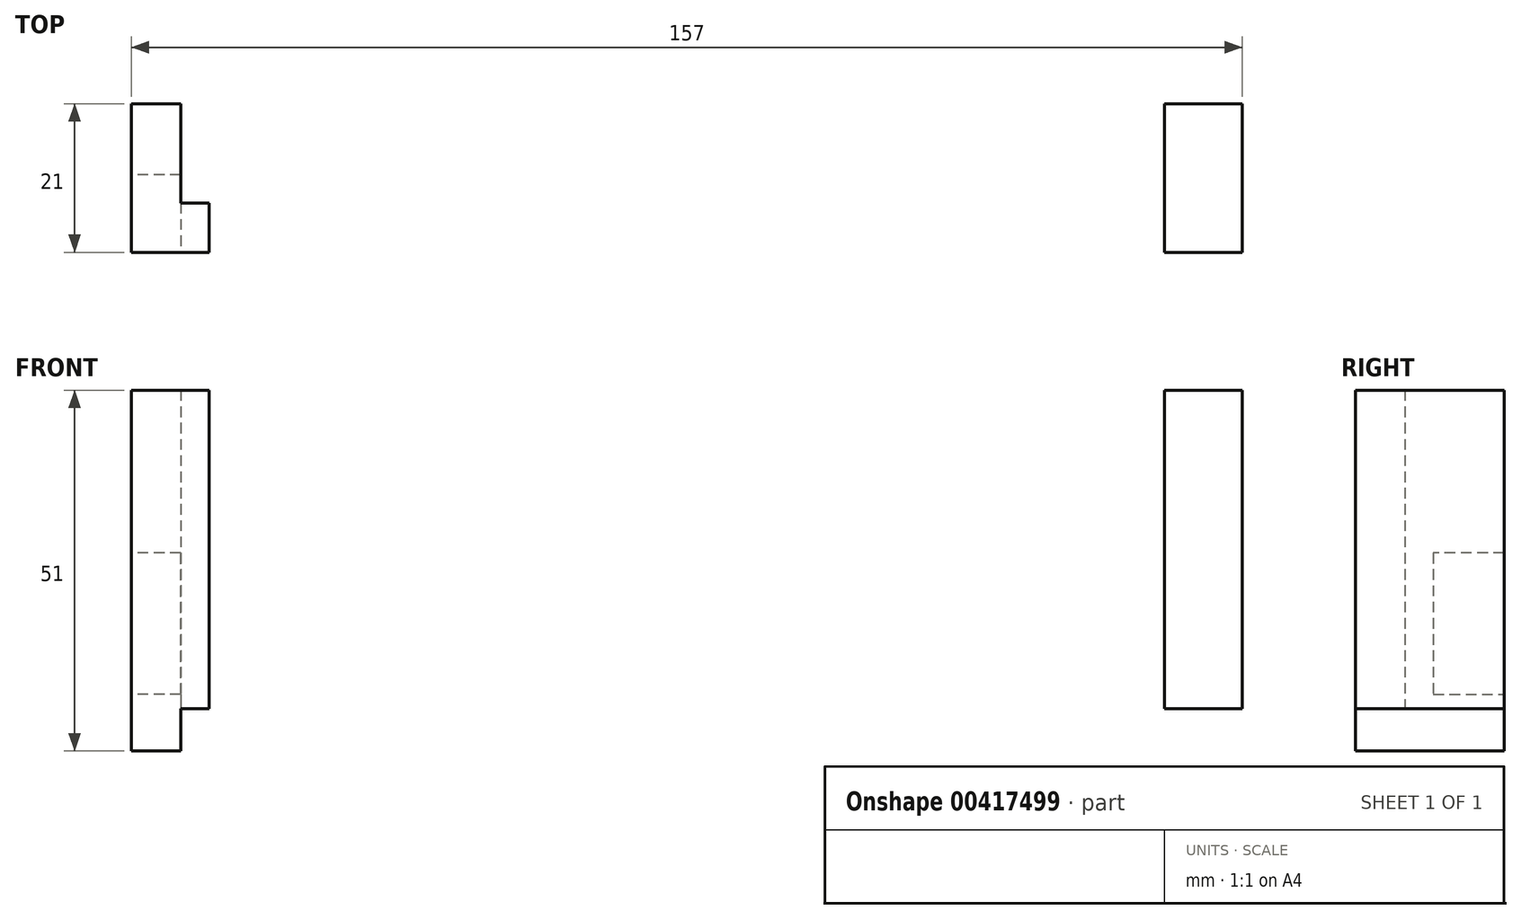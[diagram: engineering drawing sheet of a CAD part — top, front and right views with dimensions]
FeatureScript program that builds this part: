
annotation { "Feature Type Name" : "Feature", "Feature Type Description" : "" }
export const myFeature = defineFeature(function(context is Context, id is Id, definition is map)
    precondition{}
    {
        {
            var Q0;
            Q0=qCreatedBy(makeId("Front.planeOp"),FACE);
            var sketch = newSketch(context, id + "F0", { "sketchPlane" : qUnion([Q0])});
            skLineSegment(sketch, "E0.bottom", {"start": v(74.5, 22.5) * mm, "end": v(-74.5, 22.5) * mm});
            skLineSegment(sketch, "E0.top", {"start": v(74.5, -22.5) * mm, "end": v(-74.5, -22.5) * mm});
            skLineSegment(sketch, "E0.left", {"start": v(74.5, 22.5) * mm, "end": v(74.5, -22.5) * mm});
            skLineSegment(sketch, "E0.right", {"start": v(-74.5, 22.5) * mm, "end": v(-74.5, -22.5) * mm});
            skPoint(sketch, "E0.middle", {"position": v(0, 0) * mm});
            skLineSegment(sketch, "E1.0", {"start": v(78.5, 22.5) * mm, "end": v(78.5, -22.5) * mm});
            skLineSegment(sketch, "E2.0", {"start": v(-78.5, 22.5) * mm, "end": v(-78.5, -22.5) * mm});
            skLineSegment(sketch, "E3", {"start": v(-78.5, -22.5) * mm, "end": v(-74.5, -22.5) * mm});
            skLineSegment(sketch, "E4", {"start": v(74.5, -22.5) * mm, "end": v(78.5, -22.5) * mm});
            skLineSegment(sketch, "E5", {"start": v(78.5, 22.5) * mm, "end": v(74.5, 22.5) * mm});
            skLineSegment(sketch, "E6", {"start": v(-74.5, 22.5) * mm, "end": v(-78.5, 22.5) * mm});
            skLineSegment(sketch, "E7", {"start": v(0, -22.5) * mm, "end": v(67.5, -22.5) * mm});
            skLineSegment(sketch, "E8", {"start": v(67.5, -22.5) * mm, "end": v(67.5, 22.5) * mm});
            skLineSegment(sketch, "E9", {"start": v(0, -22.5) * mm, "end": v(-67.5, -22.5) * mm});
            skLineSegment(sketch, "E10", {"start": v(-67.5, -22.5) * mm, "end": v(-67.5, 22.5) * mm});
            skSolve(sketch);
        }
        {
            var Q0;
            Q0=makeQuery(id+"F0.imprint","IMPRINT",FACE,{"disambiguationData":[TD([[makeQuery(id+"F0.imprint","IMPRINT",EDGE,{"derivedFrom":sQuery(id+"F0.wireOp",EDGE,"E0.bottom")}),1.0]])]});
            var Q1;
            Q1=makeQuery(id+"F0.imprint","IMPRINT",FACE,{"disambiguationData":[TD([[makeQuery(id+"F0.imprint","IMPRINT",EDGE,{"derivedFrom":sQuery(id+"F0.wireOp",EDGE,"E0.right")}),-1.0]])]});
            var Q2;
            Q2=makeQuery(id+"F0.imprint","IMPRINT",FACE,{"disambiguationData":[TD([[makeQuery(id+"F0.imprint","IMPRINT",EDGE,{"derivedFrom":sQuery(id+"F0.wireOp",EDGE,"E0.left")}),1.0]])]});
            var Q3;
            Q3=makeQuery(id+"F0.imprint","IMPRINT",FACE,{"disambiguationData":[TD([[makeQuery(id+"F0.imprint","IMPRINT",EDGE,{"derivedFrom":sQuery(id+"F0.wireOp",EDGE,"E7")}),1.0]])]});
            extrude(context, id + "F1", {"entities" : qUnion([Q0, Q1, Q2, Q3]), "oppositeDirection" : true, "depth" : 18 * mm});
        }
        {
            var Q0;
            Q0=makeQuery(id+"F1.opExtrude","SWEPT_FACE",FACE,{"disambiguationData":[OSD([sQuery(id+"F0.wireOp",EDGE,"E0.top")])]});
            var sketch = newSketch(context, id + "F2", { "sketchPlane" : qUnion([Q0])});
            skLineSegment(sketch, "E11", {"start": v(-78.5, -9) * mm, "end": v(-74.5, -9) * mm, "construction": true});
            skLineSegment(sketch, "E12", {"start": v(78.5, -9) * mm, "end": v(74.5, -9) * mm, "construction": true});
            skLineSegment(sketch, "E13", {"start": v(74.5, 0) * mm, "end": v(74.5, -18) * mm, "construction": true});
            skLineSegment(sketch, "E14", {"start": v(-74.5, -18) * mm, "end": v(-74.5, 0) * mm, "construction": true});
            skLineSegment(sketch, "E15", {"start": v(74.5, -18) * mm, "end": v(71.5, -18) * mm});
            skLineSegment(sketch, "E16", {"start": v(71.5, -18) * mm, "end": v(71.5, 0) * mm});
            skLineSegment(sketch, "E17", {"start": v(-74.5, -18) * mm, "end": v(-71.5, -18) * mm});
            skLineSegment(sketch, "E18", {"start": v(-71.5, -18) * mm, "end": v(-71.5, 0) * mm});
            skLineSegment(sketch, "E19", {"start": v(-74.5, -18) * mm, "end": v(-74.5, -4) * mm, "construction": true});
            skLineSegment(sketch, "E20", {"start": v(-74.5, -4) * mm, "end": v(-71.5, -4) * mm, "construction": true});
            skLineSegment(sketch, "E21", {"start": v(-71.5, -4) * mm, "end": v(71.5, -4) * mm});
            skSolve(sketch);
        }
        {
            var Q0;
            {var subQ3=sQuery(id+"F2.wireOp",EDGE,"E21");Q0=makeQuery(id+"F2.imprint","IMPRINT",FACE,{"disambiguationData":[TD([[makeQuery(id+"F2.imprint","IMPRINT",EDGE,{"derivedFrom":subQ3}),-1.0]])]});}
            extrude(context, id + "F3", {"entities" : qUnion([Q0]), "operationType" : NewBodyOperationType.REMOVE, "oppositeDirection" : true, "depth" : 55 * mm});
        }
        {
            var Q0;
            {var subQ7=sQuery(id+"F2.wireOp",EDGE,"E17");Q0=makeQuery(id+"F2.imprint","IMPRINT",FACE,{"disambiguationData":[TD([[makeQuery(id+"F2.imprint","IMPRINT",EDGE,{"derivedFrom":subQ7}),-1.0]])]});}
            extrude(context, id + "F4", {"entities" : qUnion([Q0]), "operationType" : NewBodyOperationType.ADD, "depth" : 6 * mm});
        }
        {
            var Q0;
            {var subQ0=sQuery(id+"F0.wireOp",EDGE,"E2.0");Q0=makeQuery(id+"F4.boolean.opBoolean","MERGE",FACE,{"derivedFrom":[makeQuery(id+"F1.opExtrude","SWEPT_FACE",FACE,{"disambiguationData":[OSD([subQ0])]}),makeQuery(id+"F4.opExtrude","SWEPT_FACE",FACE,{"disambiguationData":[OSD([subQ0,sQuery(id+"F0.wireOp",EDGE,"E3")])]})]});}
            var sketch = newSketch(context, id + "F5", { "sketchPlane" : qUnion([Q0])});
            skLineSegment(sketch, "E22", {"start": v(-18, -28.5) * mm, "end": v(-18, -20.5) * mm, "construction": true});
            skLineSegment(sketch, "E23", {"start": v(-18, -20.5) * mm, "end": v(0, -20.5) * mm, "construction": true});
            skLineSegment(sketch, "E24", {"start": v(-18, -20.5) * mm, "end": v(-18, -0.5) * mm});
            skLineSegment(sketch, "E25", {"start": v(-18, -0.5) * mm, "end": v(-8, -0.5) * mm});
            skLineSegment(sketch, "E26", {"start": v(-8, -0.5) * mm, "end": v(-8, -20.5) * mm});
            skPoint(sketch, "E26.endSnap0", {"position": v(-9, -20.5) * mm});
            skLineSegment(sketch, "E27", {"start": v(-8, -20.5) * mm, "end": v(-18, -20.5) * mm});
            skSolve(sketch);
        }
        {
            var Q0;
            Q0=makeQuery(id+"F5.imprint","IMPRINT",FACE,{"disambiguationData":[TD([[makeQuery(id+"F5.imprint","IMPRINT",EDGE,{"derivedFrom":sQuery(id+"F5.wireOp",EDGE,"E24")}),1.0]])]});
            extrude(context, id + "F6", {"entities" : qUnion([Q0]), "operationType" : NewBodyOperationType.REMOVE, "oppositeDirection" : true, "depth" : 25 * mm});
        }
        {
            var Q0;
            {var subQ0=sQuery(id+"F0.wireOp",EDGE,"E0.left");Q0=makeQuery(id+"F0.imprint","IMPRINT",FACE,{"disambiguationData":[TD([[makeQuery(id+"F0.imprint","IMPRINT",EDGE,{"derivedFrom":subQ0}),-1.0]])]});}
            var Q1;
            Q1=makeQuery(id+"F0.imprint","IMPRINT",FACE,{"disambiguationData":[TD([[makeQuery(id+"F0.imprint","IMPRINT",EDGE,{"derivedFrom":sQuery(id+"F0.wireOp",EDGE,"E0.left")}),1.0]])]});
            var Q2;
            {var subQ0=sQuery(id+"F0.wireOp",EDGE,"E0.right");Q2=makeQuery(id+"F0.imprint","IMPRINT",FACE,{"disambiguationData":[TD([[makeQuery(id+"F0.imprint","IMPRINT",EDGE,{"derivedFrom":subQ0}),1.0]])]});}
            var Q3;
            Q3=makeQuery(id+"F0.imprint","IMPRINT",FACE,{"disambiguationData":[TD([[makeQuery(id+"F0.imprint","IMPRINT",EDGE,{"derivedFrom":sQuery(id+"F0.wireOp",EDGE,"E0.right")}),-1.0]])]});
            extrude(context, id + "F7", {"entities" : qUnion([Q0, Q1, Q2, Q3]), "depth" : 3 * mm});
        }
        {
            var Q0;
            Q0=makeQuery(id+"F7.opExtrude","SWEPT_BODY",BODY,{"disambiguationData":[OSD([sQuery(id+"F0.wireOp",EDGE,"E0.bottom"),sQuery(id+"F0.wireOp",EDGE,"E0.top"),sQuery(id+"F0.wireOp",EDGE,"E1.0"),sQuery(id+"F0.wireOp",EDGE,"E4"),sQuery(id+"F0.wireOp",EDGE,"E5"),sQuery(id+"F0.wireOp",EDGE,"E8")])]});
            var Q1;
            Q1=makeQuery(id+"F1.opExtrude","SWEPT_BODY",BODY,{"disambiguationData":[OSD([sQuery(id+"F0.wireOp",EDGE,"E0.bottom"),sQuery(id+"F0.wireOp",EDGE,"E0.top"),sQuery(id+"F0.wireOp",EDGE,"E1.0"),sQuery(id+"F0.wireOp",EDGE,"E2.0"),sQuery(id+"F0.wireOp",EDGE,"E3"),sQuery(id+"F0.wireOp",EDGE,"E4"),sQuery(id+"F0.wireOp",EDGE,"E5"),sQuery(id+"F0.wireOp",EDGE,"E6"),sQuery(id+"F0.wireOp",EDGE,"E7"),sQuery(id+"F0.wireOp",EDGE,"E9")])]});
            var Q2;
            Q2=makeQuery(id+"F7.opExtrude","SWEPT_BODY",BODY,{"disambiguationData":[OSD([sQuery(id+"F0.wireOp",EDGE,"E0.bottom"),sQuery(id+"F0.wireOp",EDGE,"E0.top"),sQuery(id+"F0.wireOp",EDGE,"E2.0"),sQuery(id+"F0.wireOp",EDGE,"E3"),sQuery(id+"F0.wireOp",EDGE,"E6"),sQuery(id+"F0.wireOp",EDGE,"E10")])]});
            booleanBodies(context, id + "F8", {"operationType" : BooleanOperationType.UNION, "tools" : qUnion([Q0, Q1, Q2])});
        }
        {
            var Q0;
            {var subQ1=sQuery(id+"F0.wireOp",EDGE,"E9");var subQ2=sQuery(id+"F0.wireOp",EDGE,"E7");var subQ3=sQuery(id+"F0.wireOp",EDGE,"E4");var subQ4=sQuery(id+"F0.wireOp",EDGE,"E3");var subQ5=sQuery(id+"F0.wireOp",EDGE,"E2.0");var subQ6=sQuery(id+"F0.wireOp",EDGE,"E0.top");Q0=makeQuery(id+"F8.opBoolean","SPLIT",FACE,{"disambiguationData":[TD([makeQuery(id+"F1.opExtrude","SWEPT_FACE",FACE,{"disambiguationData":[OSD([subQ5])]})])],"derivedFrom":makeQuery(id+"F4.boolean.opBoolean","MERGE",FACE,{"derivedFrom":[makeQuery(id+"F1.opExtrude","CAP_FACE",FACE,{"disambiguationData":[OSD([sQuery(id+"F0.wireOp",EDGE,"E0.bottom"),subQ6,sQuery(id+"F0.wireOp",EDGE,"E1.0"),subQ5,subQ4,subQ3,sQuery(id+"F0.wireOp",EDGE,"E5"),sQuery(id+"F0.wireOp",EDGE,"E6"),subQ2,subQ1])],"isStart":true}),makeQuery(id+"F4.opExtrude","SWEPT_FACE",FACE,{"disambiguationData":[OSD([subQ6,subQ4,subQ3,subQ2,subQ1])]})]})});}
            var sketch = newSketch(context, id + "F9", { "sketchPlane" : qUnion([Q0])});
            skLineSegment(sketch, "E28", {"start": v(-78.5, -28.5) * mm, "end": v(-71.5, -28.5) * mm});
            skLineSegment(sketch, "E29", {"start": v(-71.5, -28.5) * mm, "end": v(-71.5, -22.5) * mm});
            skLineSegment(sketch, "E30", {"start": v(-71.5, -22.5) * mm, "end": v(-78.5, -22.5) * mm});
            skLineSegment(sketch, "E31", {"start": v(-78.5, -22.5) * mm, "end": v(-78.5, -28.5) * mm});
            skSolve(sketch);
        }
        {
            var Q0;
            Q0=makeQuery(id+"F9.imprint","IMPRINT",FACE,{"disambiguationData":[TD([[makeQuery(id+"F9.imprint","IMPRINT",EDGE,{"derivedFrom":sQuery(id+"F9.wireOp",EDGE,"E28")}),-1.0]])]});
            extrude(context, id + "F10", {"entities" : qUnion([Q0]), "operationType" : NewBodyOperationType.ADD, "depth" : 3 * mm});
        }
    });
